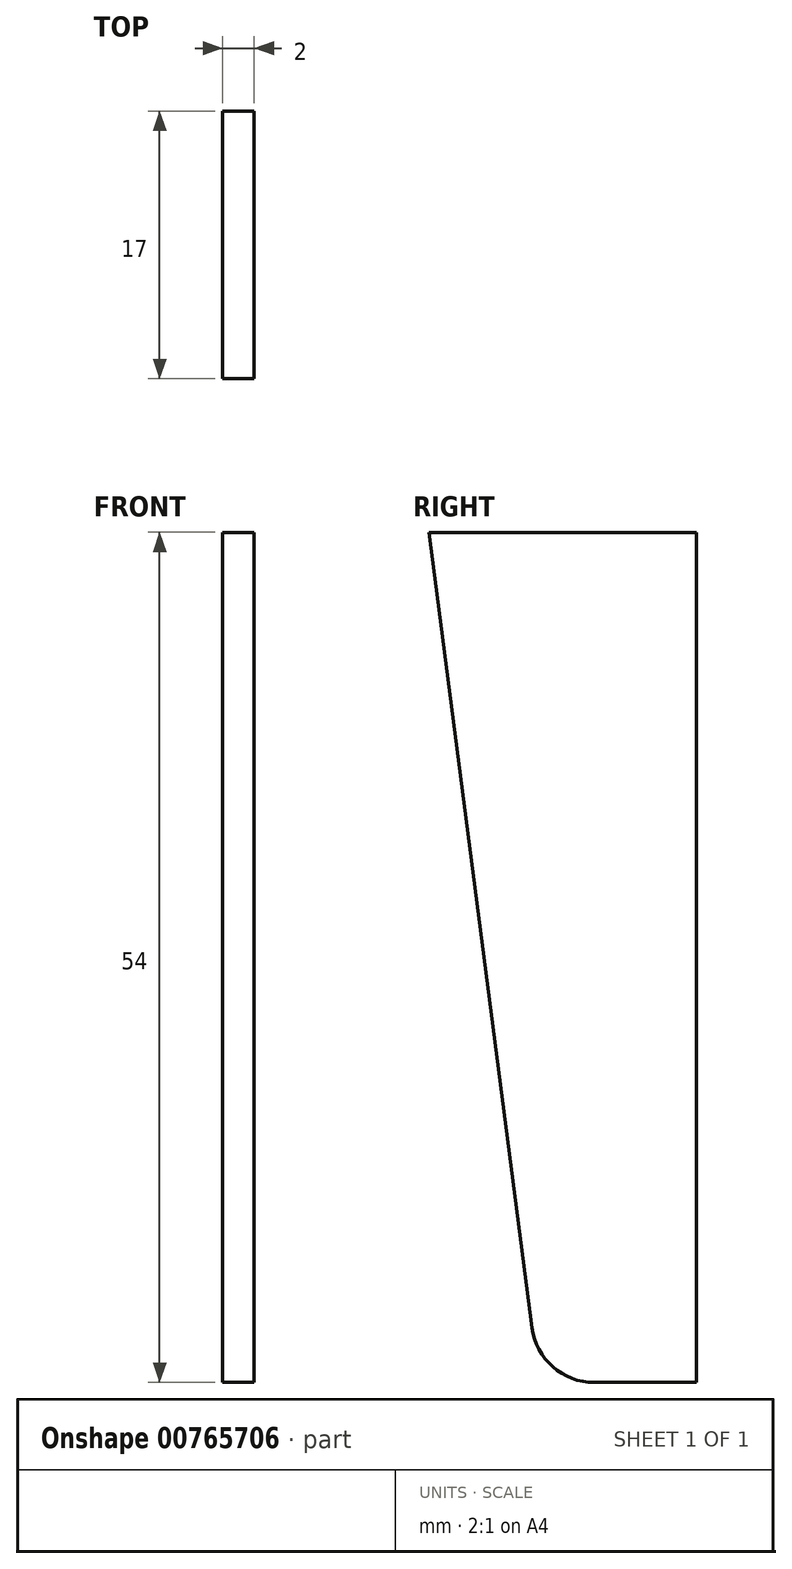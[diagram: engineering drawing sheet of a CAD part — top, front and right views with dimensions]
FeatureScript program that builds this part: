
annotation { "Feature Type Name" : "Feature", "Feature Type Description" : "" }
export const myFeature = defineFeature(function(context is Context, id is Id, definition is map)
    precondition{}
    {
        {
            var Q0;
            Q0=qCreatedBy(makeId("Right.planeOp"),FACE);
            var sketch = newSketch(context, id + "F0", { "sketchPlane" : qUnion([Q0])});
            skLineSegment(sketch, "E0", {"start": v(44.05, 31.1) * mm, "end": v(44.05, -22.9) * mm});
            skLineSegment(sketch, "E1", {"start": v(44.05, 31.1) * mm, "end": v(27.05, 31.1) * mm});
            skLineSegment(sketch, "E2", {"start": v(44.05, -22.9) * mm, "end": v(37.57, -22.9) * mm});
            skLineSegment(sketch, "E3", {"start": v(27.05, 31.1) * mm, "end": v(33.6, -19.4) * mm});
            skPoint(sketch, "E4.visualSharp", {"position": v(34.05, -22.9) * mm});
            skArc(sketch, "E4.filletArc", {"start": v(33.6, -19.4) * mm, "mid": v(34.93, -21.9) * mm, "end": v(37.57, -22.9) * mm});
            skSolve(sketch);
        }
        {
            var Q0;
            Q0=makeQuery(id+"F0.imprint","IMPRINT",FACE,{"disambiguationData":[TD([[makeQuery(id+"F0.imprint","IMPRINT",EDGE,{"derivedFrom":sQuery(id+"F0.wireOp",EDGE,"E0")}),-1.0]])]});
            extrude(context, id + "F1", {"entities" : qUnion([Q0]), "depth" : 2 * mm, "offsetDistance" : 25 * mm});
        }
    });
